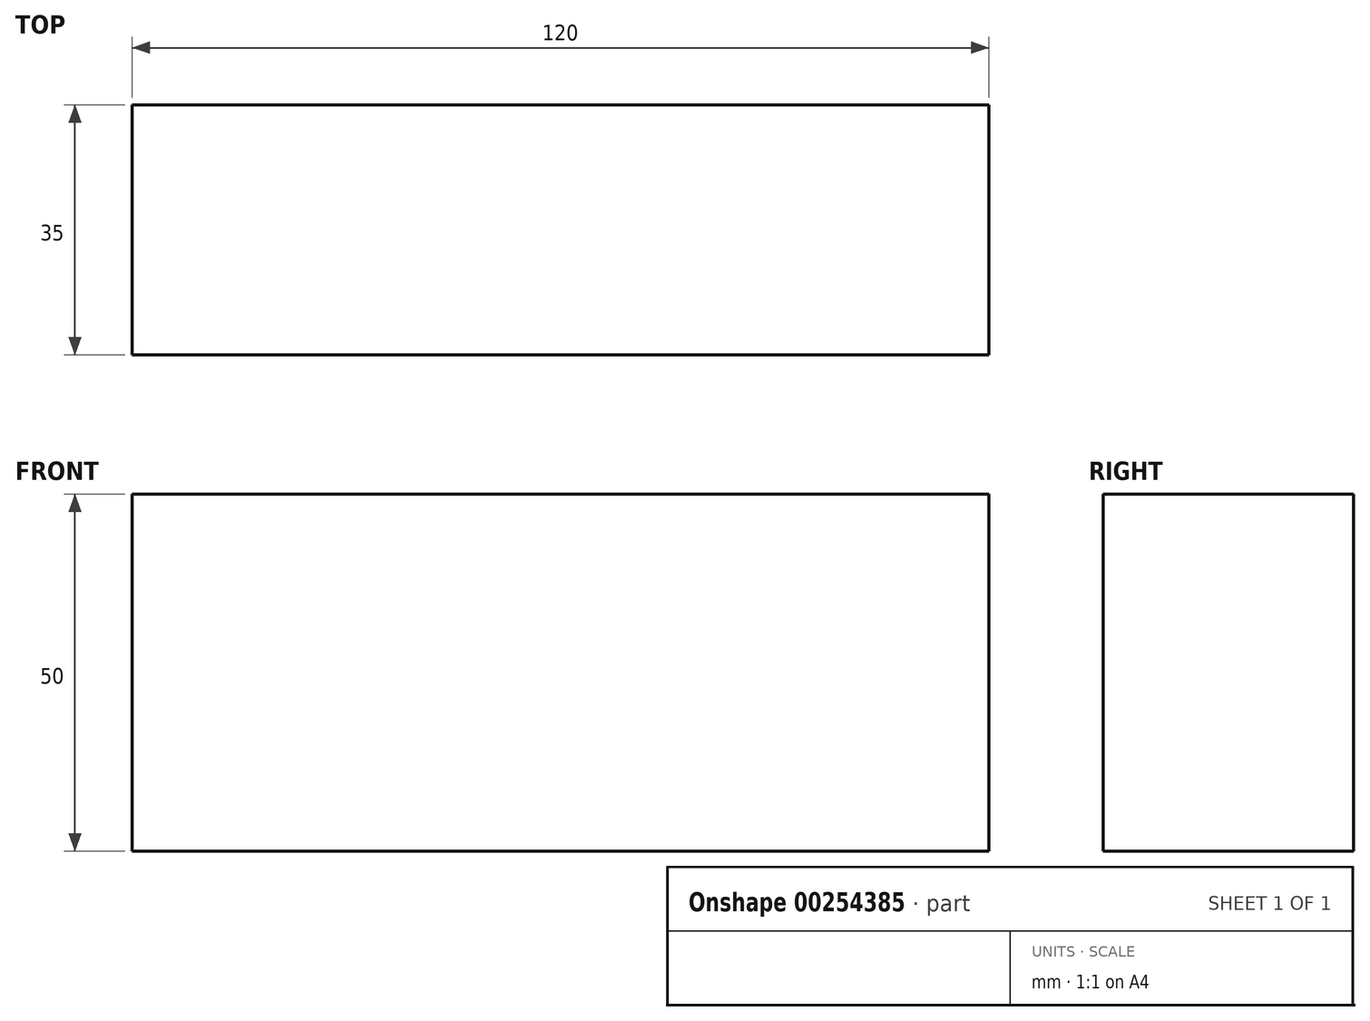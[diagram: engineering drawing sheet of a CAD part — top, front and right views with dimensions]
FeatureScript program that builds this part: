
annotation { "Feature Type Name" : "Feature", "Feature Type Description" : "" }
export const myFeature = defineFeature(function(context is Context, id is Id, definition is map)
    precondition{}
    {
        {
            var Q0;
            Q0=qCreatedBy(makeId("Top.planeOp"),FACE);
            var sketch = newSketch(context, id + "F0", { "sketchPlane" : qUnion([Q0])});
            skLineSegment(sketch, "E0.bottom", {"start": v(-60, 17.5) * mm, "end": v(60, 17.5) * mm});
            skLineSegment(sketch, "E0.top", {"start": v(-60, -17.5) * mm, "end": v(60, -17.5) * mm});
            skLineSegment(sketch, "E0.left", {"start": v(-60, 17.5) * mm, "end": v(-60, -17.5) * mm});
            skLineSegment(sketch, "E0.right", {"start": v(60, 17.5) * mm, "end": v(60, -17.5) * mm});
            skPoint(sketch, "E0.middle", {"position": v(0, 0) * mm});
            skSolve(sketch);
        }
        {
            var Q0;
            Q0 = qSketchRegion(id + "F0", true);
            extrude(context, id + "F1", {"entities" : qUnion([Q0]), "depth" : 25 * mm});
        }
        {
            var Q0;
            Q0=makeQuery(id+"F1.opExtrude","CAP_FACE",FACE,{"disambiguationData":[OSD([sQuery(id+"F0.wireOp",EDGE,"E0.bottom"),sQuery(id+"F0.wireOp",EDGE,"E0.top"),sQuery(id+"F0.wireOp",EDGE,"E0.left"),sQuery(id+"F0.wireOp",EDGE,"E0.right")])],"isStart":false});
            extrude(context, id + "F2", {"entities" : qUnion([Q0]), "operationType" : NewBodyOperationType.ADD, "depth" : 25 * mm});
        }
    });
